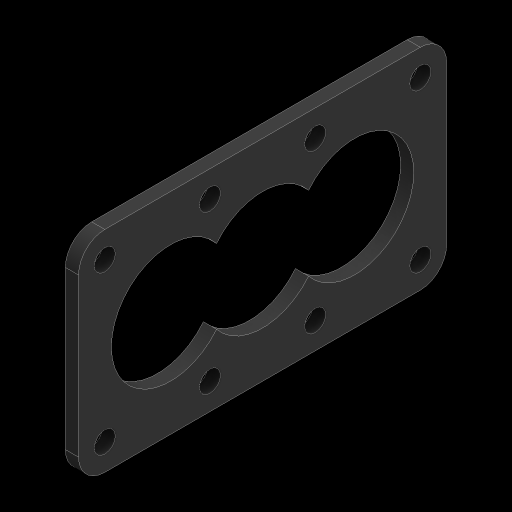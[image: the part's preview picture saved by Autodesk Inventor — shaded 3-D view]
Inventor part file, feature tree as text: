
AUTODESK INVENTOR PART (.ipt)
format: ipt  version: 2024 (Build 280153000, 153)  size: 146,432 bytes
history: native  units: in
note: dims shown in document units (in); Inventor stores cm internally (conversion verified against a paired STEP export)
features: sketch x3, hole x2, pattern_linear x2, extrude x1, fillet x1
ambient origin geometry x8: Origin, YZ Plane, XZ Plane, XY Plane, X Axis, Y Axis, Z Axis, Center Point
bodies: Solid1 (feature_tree)
feature tree (9):
  extrude  "RECTANGLE"  Depth=7.0in
  fillet  "Fillet1"  Radius=0.25in
  hole  "Hole1"  [1 undecoded]
  pattern_linear  "SMALL HOLES"  Count1=2 Spacing1=3.0in
  hole  "Hole2"  [1 undecoded]
  pattern_linear  "LARGE HOLES"  Spacing1=0.0in  [1 undecoded]
  sketch  "Sketch1"  dims[d0=4.0in d1=7.0in d2=0.25in d3=0.0in]
  sketch  "Sketch2"  dims[d4=0.5in]
  sketch  "Sketch3"  dims[d5=0.4in d6=0.75in d7=0.375in d8=0.25in d9=0.5635in d10=1.0in d11=0.8108in d12=1.5748in d14=2.0in d15=0.7874in d17=3.0in d18=2.25in d19=0.75in d20=0.375in d21=0.25in d22=0.5635in d23=1.0in d24=0.8108in d25=1.75in d26=0.0in d27=1.1811in d29=1.75in]
note: 3 required parameter values undecoded (feature->parameter linkage not recoverable at this tier; creation-order binding heuristic only, values carry confidence <= 0.55)
